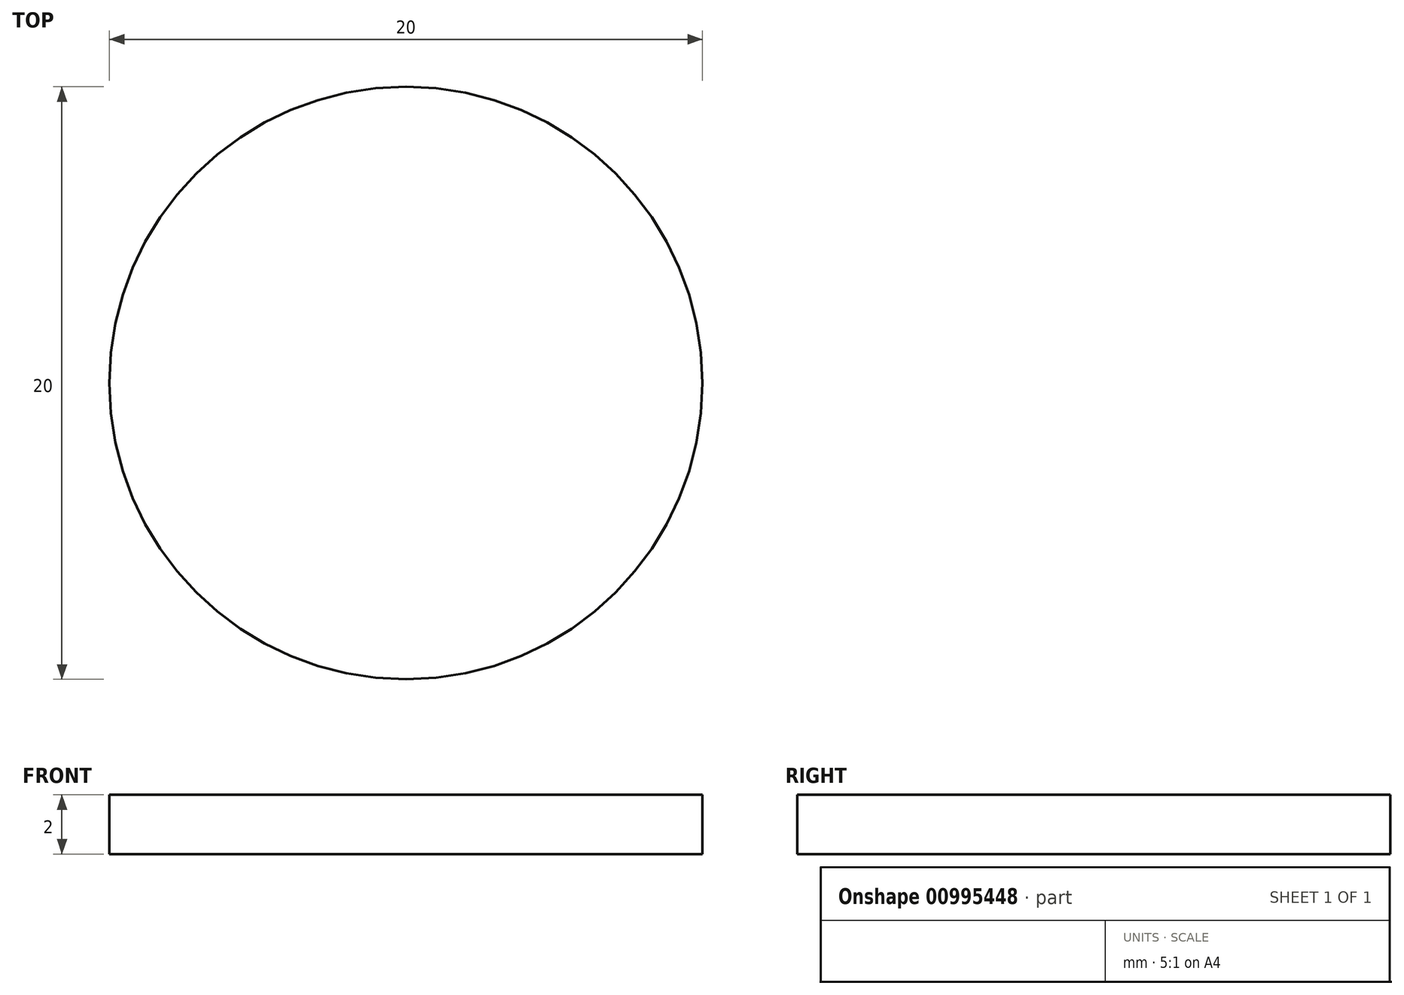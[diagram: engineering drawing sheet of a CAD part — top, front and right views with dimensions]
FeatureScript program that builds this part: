
annotation { "Feature Type Name" : "Feature", "Feature Type Description" : "" }
export const myFeature = defineFeature(function(context is Context, id is Id, definition is map)
    precondition{}
    {
        {
            var Q0;
            Q0=qCreatedBy(makeId("Top.planeOp"),FACE);
            var sketch = newSketch(context, id + "F0", { "sketchPlane" : qUnion([Q0])});
            skCircle(sketch, "E0", {"center": v(0, 0) * mm, "radius": 10 * mm});
            skSolve(sketch);
        }
        {
            var Q0;
            Q0 = qSketchRegion(id + "F0", true);
            extrude(context, id + "F1", {"entities" : qUnion([Q0]), "depth" : 2 * mm, "offsetDistance" : 25 * mm});
        }
    });
